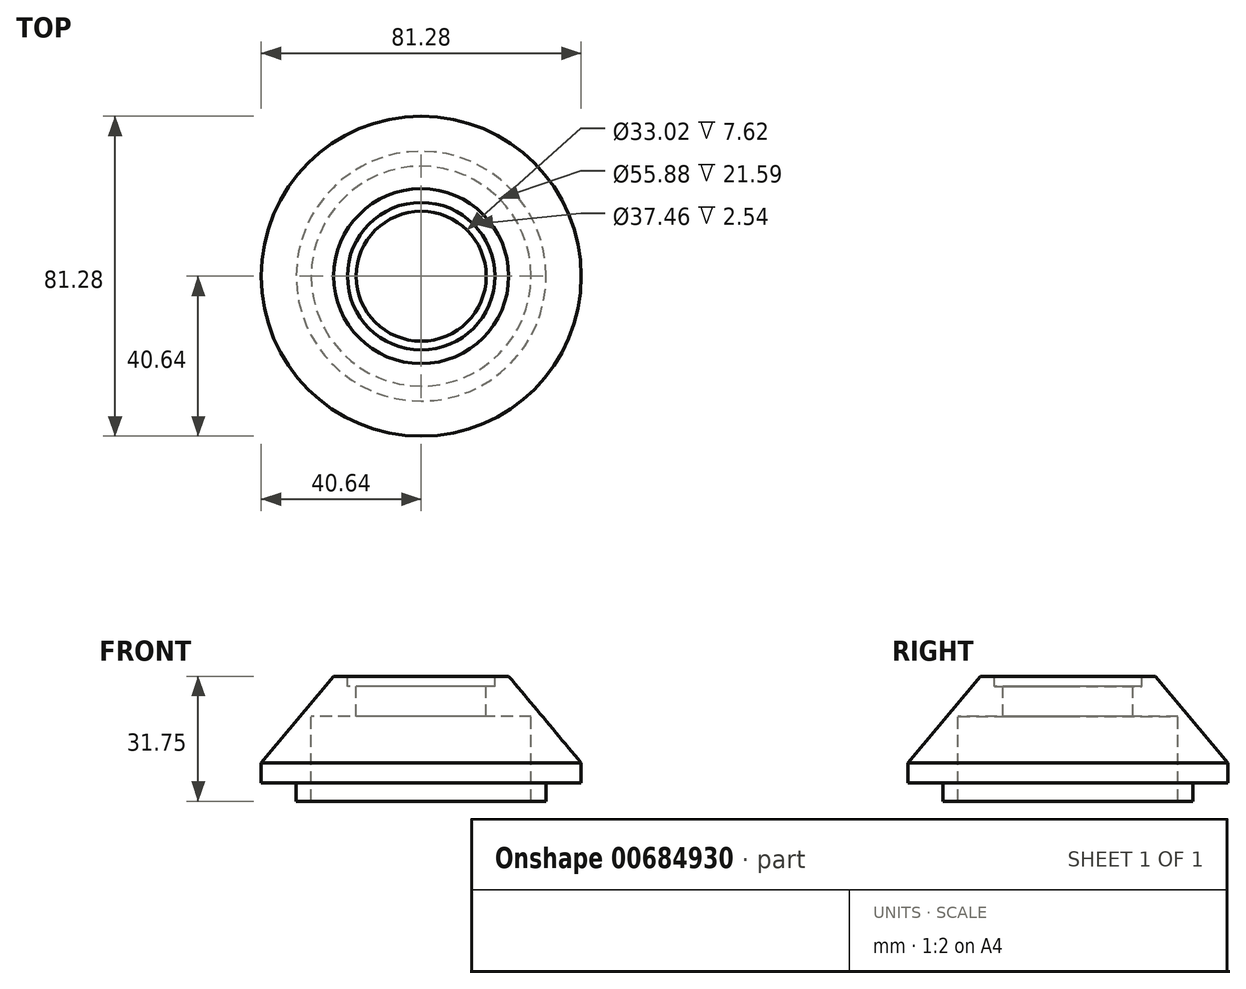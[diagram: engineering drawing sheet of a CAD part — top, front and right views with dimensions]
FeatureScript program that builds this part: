
annotation { "Feature Type Name" : "Feature", "Feature Type Description" : "" }
export const myFeature = defineFeature(function(context is Context, id is Id, definition is map)
    precondition{}
    {
        {
            var Q0;
            Q0=qCreatedBy(makeId("Front.planeOp"),FACE);
            var sketch = newSketch(context, id + "F0", { "sketchPlane" : qUnion([Q0])});
            skLineSegment(sketch, "E0", {"start": v(0, 60.75) * mm, "end": v(0, -52.82) * mm, "construction": true});
            skLineSegment(sketch, "E1", {"start": v(16.51, 10.16) * mm, "end": v(18.73, 10.16) * mm});
            skLineSegment(sketch, "E2", {"start": v(18.73, 10.16) * mm, "end": v(18.73, 12.7) * mm});
            skLineSegment(sketch, "E3", {"start": v(18.73, 12.7) * mm, "end": v(22.23, 12.7) * mm});
            skLineSegment(sketch, "E4", {"start": v(22.23, 12.7) * mm, "end": v(40.64, -9.27) * mm});
            skLineSegment(sketch, "E5", {"start": v(40.64, -9.27) * mm, "end": v(40.64, -14.35) * mm});
            skLineSegment(sketch, "E6", {"start": v(40.64, -14.35) * mm, "end": v(31.75, -14.35) * mm});
            skLineSegment(sketch, "E7", {"start": v(31.75, -14.35) * mm, "end": v(31.75, -19.05) * mm});
            skLineSegment(sketch, "E8", {"start": v(31.75, -19.05) * mm, "end": v(27.94, -19.05) * mm});
            skLineSegment(sketch, "E9", {"start": v(27.94, -19.05) * mm, "end": v(27.94, 2.54) * mm});
            skLineSegment(sketch, "E10", {"start": v(27.94, 2.54) * mm, "end": v(16.51, 2.54) * mm});
            skLineSegment(sketch, "E11", {"start": v(16.51, 10.16) * mm, "end": v(16.51, 2.54) * mm});
            skSolve(sketch);
        }
        {
            var Q0;
            Q0 = qSketchRegion(id + "F0", true);
            var Q1;
            Q1=sQuery(id+"F0.wireOp",EDGE,"E0");
            revolve(context, id + "F1", {"surfaceOperationType" : NewSurfaceOperationType.NEW, "entities" : qUnion([Q0]), "axis" : qUnion([Q1]), "revolveType" : RevolveType.FULL});
        }
    });
